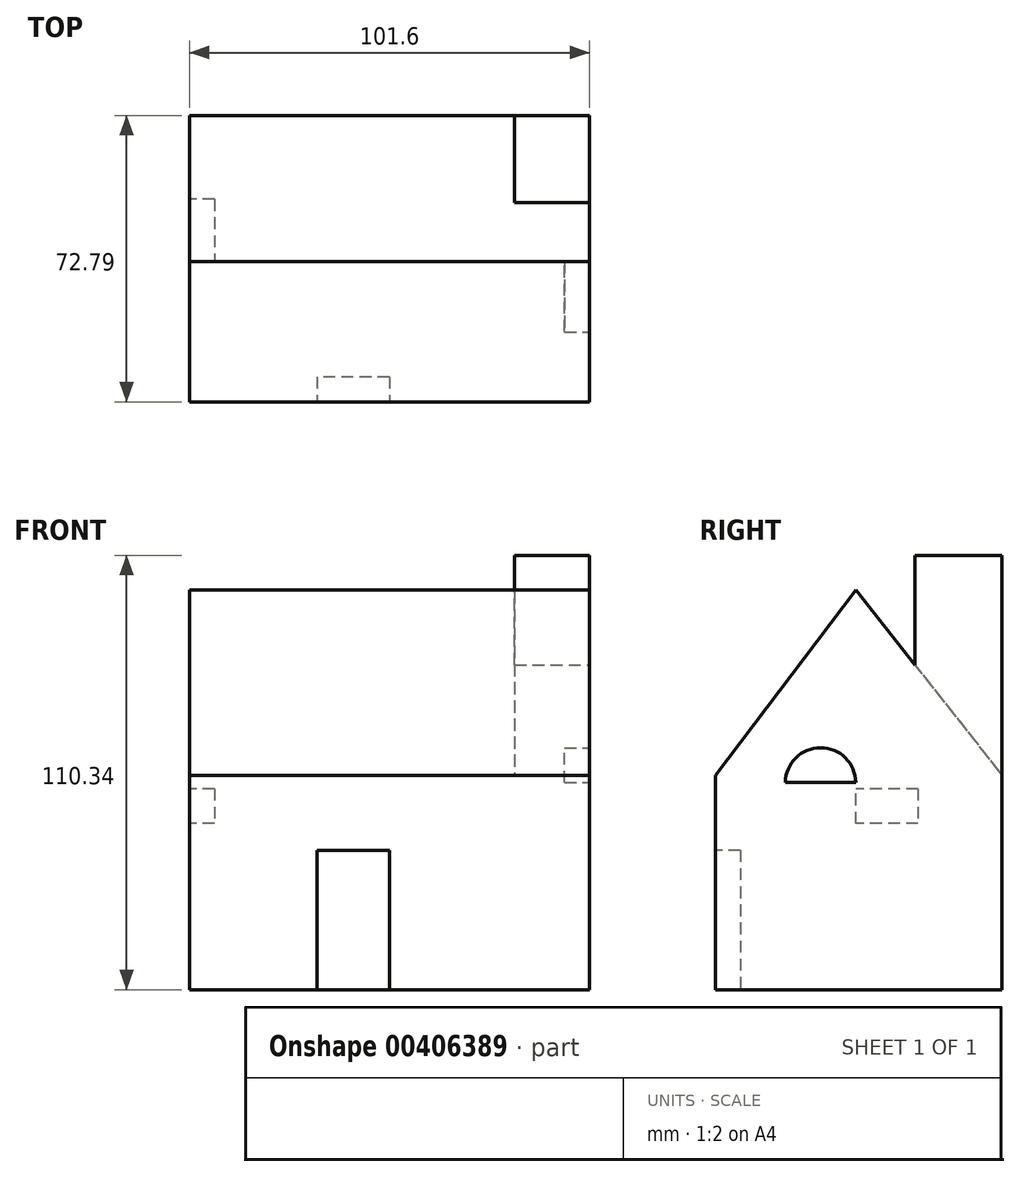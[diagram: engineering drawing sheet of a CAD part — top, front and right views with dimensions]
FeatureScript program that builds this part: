
annotation { "Feature Type Name" : "Feature", "Feature Type Description" : "" }
export const myFeature = defineFeature(function(context is Context, id is Id, definition is map)
    precondition{}
    {
        {
            var Q0;
            Q0=qCreatedBy(makeId("Right.planeOp"),FACE);
            var sketch = newSketch(context, id + "F0", { "sketchPlane" : qUnion([Q0])});
            skLineSegment(sketch, "E0.top", {"start": v(-35.68, 0) * mm, "end": v(37.11, 0) * mm});
            skLineSegment(sketch, "E0.left", {"start": v(-35.68, 54.48) * mm, "end": v(-35.68, 0) * mm});
            skLineSegment(sketch, "E0.right", {"start": v(37.11, 54.48) * mm, "end": v(37.11, 0) * mm});
            skLineSegment(sketch, "E1", {"start": v(0, 101.58) * mm, "end": v(37.11, 54.48) * mm});
            skLineSegment(sketch, "E2", {"start": v(0, 101.58) * mm, "end": v(-35.68, 54.48) * mm});
            skSolve(sketch);
        }
        {
            var Q0;
            Q0 = qSketchRegion(id + "F0", true);
            extrude(context, id + "F1", {"entities" : qUnion([Q0]), "depth" : 50.8 * mm, "hasSecondDirection" : true, "secondDirectionOppositeDirection" : true, "secondDirectionDepth" : 50.8 * mm});
        }
        {
            var Q0;
            Q0=makeQuery(id+"F1.opExtrude","CAP_FACE",FACE,{"disambiguationData":[OSD([sQuery(id+"F0.wireOp",EDGE,"E0.top"),sQuery(id+"F0.wireOp",EDGE,"E0.left"),sQuery(id+"F0.wireOp",EDGE,"E0.right"),sQuery(id+"F0.wireOp",EDGE,"E1"),sQuery(id+"F0.wireOp",EDGE,"E2")])],"isStart":false});
            var sketch = newSketch(context, id + "F2", { "sketchPlane" : qUnion([Q0])});
            skLineSegment(sketch, "E3", {"start": v(15, 82.55) * mm, "end": v(15, 110.34) * mm});
            skLineSegment(sketch, "E4", {"start": v(15, 110.34) * mm, "end": v(37.11, 110.34) * mm});
            skLineSegment(sketch, "E5", {"start": v(37.11, 110.34) * mm, "end": v(37.11, 54.48) * mm});
            skLineSegment(sketch, "E6", {"start": v(15, 82.55) * mm, "end": v(37.11, 54.48) * mm});
            skSolve(sketch);
        }
        {
            var Q0;
            Q0=makeQuery(id+"F2.imprint","IMPRINT",FACE,{"disambiguationData":[TD([[makeQuery(id+"F2.imprint","IMPRINT",EDGE,{"derivedFrom":sQuery(id+"F2.wireOp",EDGE,"E3")}),-1.0]])]});
            extrude(context, id + "F3", {"entities" : qUnion([Q0]), "operationType" : NewBodyOperationType.ADD, "oppositeDirection" : true, "depth" : 19.05 * mm});
        }
        {
            var Q0;
            Q0=makeQuery(id+"F1.opExtrude","SWEPT_FACE",FACE,{"disambiguationData":[OSD([sQuery(id+"F0.wireOp",EDGE,"E0.left")])]});
            var sketch = newSketch(context, id + "F4", { "sketchPlane" : qUnion([Q0])});
            skLineSegment(sketch, "E7.bottom", {"start": v(-18.42, 35.45) * mm, "end": v(0, 35.45) * mm});
            skLineSegment(sketch, "E7.top", {"start": v(-18.42, 0) * mm, "end": v(0, 0) * mm});
            skLineSegment(sketch, "E7.left", {"start": v(-18.42, 35.45) * mm, "end": v(-18.42, 0) * mm});
            skLineSegment(sketch, "E7.right", {"start": v(0, 35.45) * mm, "end": v(0, 0) * mm});
            skSolve(sketch);
        }
        {
            var Q0;
            Q0=makeQuery(id+"F4.imprint","IMPRINT",FACE,{"disambiguationData":[TD([[makeQuery(id+"F4.imprint","IMPRINT",EDGE,{"derivedFrom":sQuery(id+"F4.wireOp",EDGE,"E7.bottom")}),-1.0]])]});
            extrude(context, id + "F5", {"entities" : qUnion([Q0]), "operationType" : NewBodyOperationType.REMOVE, "oppositeDirection" : true, "depth" : 6.35 * mm});
        }
        {
            var Q0;
            Q0=makeQuery(id+"F1.opExtrude","CAP_FACE",FACE,{"disambiguationData":[OSD([sQuery(id+"F0.wireOp",EDGE,"E0.top"),sQuery(id+"F0.wireOp",EDGE,"E0.left"),sQuery(id+"F0.wireOp",EDGE,"E0.right"),sQuery(id+"F0.wireOp",EDGE,"E1"),sQuery(id+"F0.wireOp",EDGE,"E2")])],"isStart":true});
            var sketch = newSketch(context, id + "F6", { "sketchPlane" : qUnion([Q0])});
            skLineSegment(sketch, "E8", {"start": v(-15.82, 51.05) * mm, "end": v(-15.82, 42.2) * mm});
            skLineSegment(sketch, "E9", {"start": v(-15.82, 51.05) * mm, "end": v(0, 51.05) * mm});
            skLineSegment(sketch, "E10", {"start": v(-15.82, 42.2) * mm, "end": v(0, 42.2) * mm});
            skLineSegment(sketch, "E11", {"start": v(0, 42.2) * mm, "end": v(0, 51.05) * mm});
            skSolve(sketch);
        }
        {
            var Q0;
            Q0=makeQuery(id+"F6.imprint","IMPRINT",FACE,{"disambiguationData":[TD([[makeQuery(id+"F6.imprint","IMPRINT",EDGE,{"derivedFrom":sQuery(id+"F6.wireOp",EDGE,"E8")}),1.0]])]});
            extrude(context, id + "F7", {"entities" : qUnion([Q0]), "operationType" : NewBodyOperationType.REMOVE, "oppositeDirection" : true, "depth" : 6.35 * mm});
        }
        {
            var Q0;
            Q0=makeQuery(id+"F3.boolean.opBoolean","MERGE",FACE,{"derivedFrom":[makeQuery(id+"F1.opExtrude","CAP_FACE",FACE,{"disambiguationData":[OSD([sQuery(id+"F0.wireOp",EDGE,"E0.top"),sQuery(id+"F0.wireOp",EDGE,"E0.left"),sQuery(id+"F0.wireOp",EDGE,"E0.right"),sQuery(id+"F0.wireOp",EDGE,"E1"),sQuery(id+"F0.wireOp",EDGE,"E2")])],"isStart":false}),makeQuery(id+"F3.opExtrude","CAP_FACE",FACE,{"disambiguationData":[OSD([sQuery(id+"F2.wireOp",EDGE,"E3"),sQuery(id+"F2.wireOp",EDGE,"E4"),sQuery(id+"F2.wireOp",EDGE,"E5"),sQuery(id+"F2.wireOp",EDGE,"E6")])],"isStart":true})]});
            var sketch = newSketch(context, id + "F8", { "sketchPlane" : qUnion([Q0])});
            skPoint(sketch, "E12.center.orphan", {"position": v(0, 52.6) * mm});
            skArc(sketch, "E13", {"start": v(0, 52.6) * mm, "mid": v(-8.95, 61.47) * mm, "end": v(-17.9, 52.6) * mm});
            skLineSegment(sketch, "E14", {"start": v(-17.9, 52.6) * mm, "end": v(0, 52.6) * mm});
            skSolve(sketch);
        }
        {
            var Q0;
            Q0=makeQuery(id+"F8.imprint","IMPRINT",FACE,{"disambiguationData":[TD([[makeQuery(id+"F8.imprint","IMPRINT",EDGE,{"derivedFrom":sQuery(id+"F8.wireOp",EDGE,"E13")}),1.0]])]});
            extrude(context, id + "F9", {"entities" : qUnion([Q0]), "operationType" : NewBodyOperationType.REMOVE, "oppositeDirection" : true, "depth" : 6.35 * mm});
        }
    });
